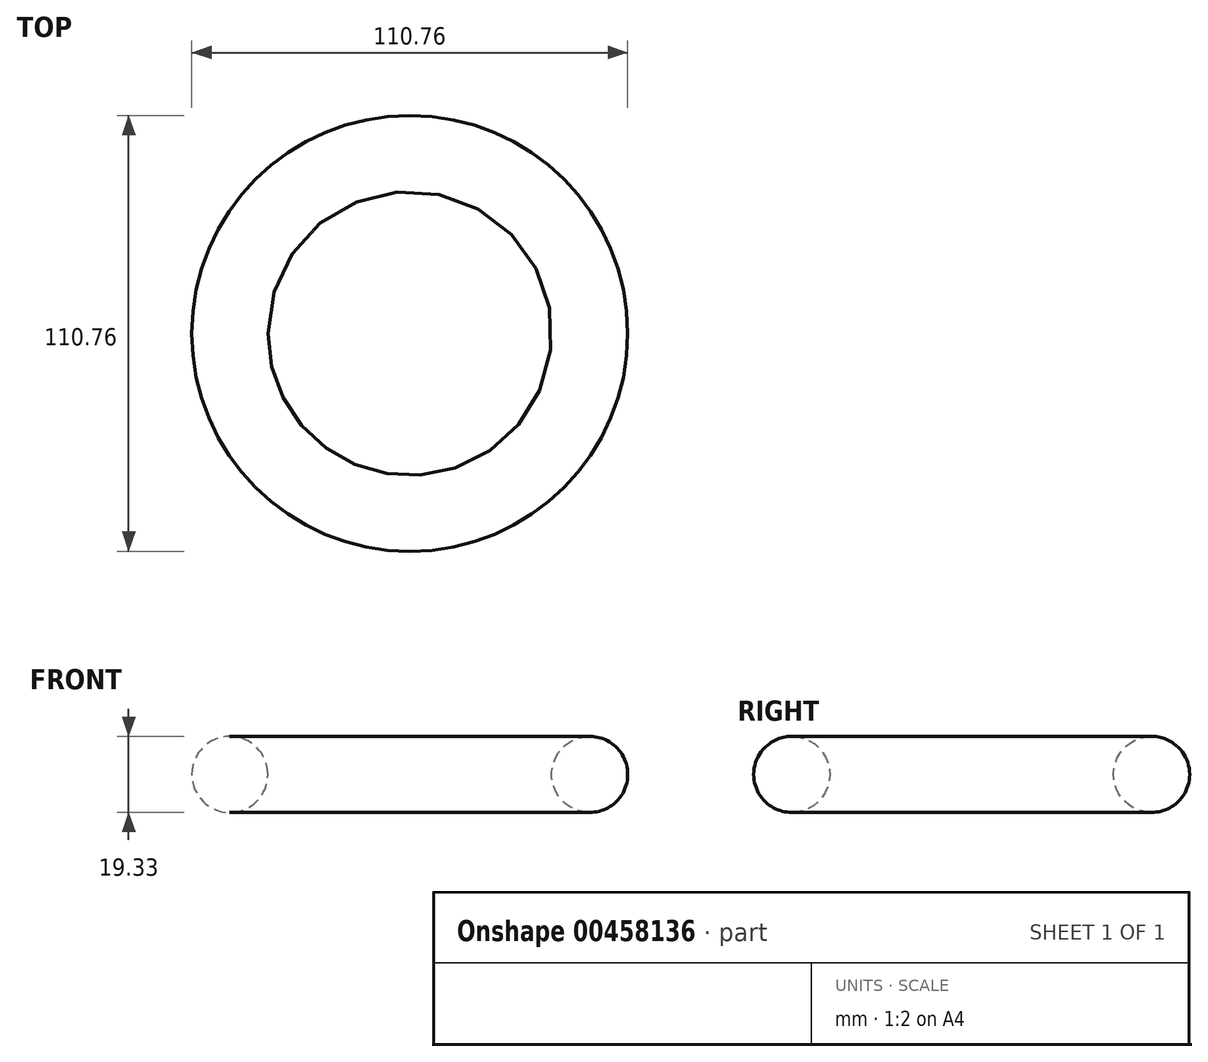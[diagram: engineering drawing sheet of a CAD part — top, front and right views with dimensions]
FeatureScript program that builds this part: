
annotation { "Feature Type Name" : "Feature", "Feature Type Description" : "" }
export const myFeature = defineFeature(function(context is Context, id is Id, definition is map)
    precondition{}
    {
        {
            var Q0;
            Q0=qCreatedBy(makeId("Top.planeOp"),FACE);
            var sketch = newSketch(context, id + "F0", { "sketchPlane" : qUnion([Q0])});
            skCircle(sketch, "E0", {"center": v(0, 0) * mm, "radius": 39.6 * mm});
            skSolve(sketch);
        }
        {
            var Q0;
            Q0=qCreatedBy(makeId("Front.planeOp"),FACE);
            var sketch = newSketch(context, id + "F1", { "sketchPlane" : qUnion([Q0])});
            skCircle(sketch, "E1", {"center": v(-45.71, -8.05) * mm, "radius": 9.66 * mm});
            skSolve(sketch);
        }
        {
            var Q0;
            Q0=makeQuery(id+"F1.imprint","IMPRINT",FACE,{"disambiguationData":[TD([[makeQuery(id+"F1.imprint","IMPRINT",EDGE,{"derivedFrom":sQuery(id+"F1.wireOp",EDGE,"E1")}),1.0]])]});
            var Q1;
            Q1=sQuery(id+"F0.wireOp",EDGE,"E0");
            revolve(context, id + "F2", {"entities" : qUnion([Q0]), "axis" : qUnion([Q1]), "revolveType" : RevolveType.FULL});
        }
    });
